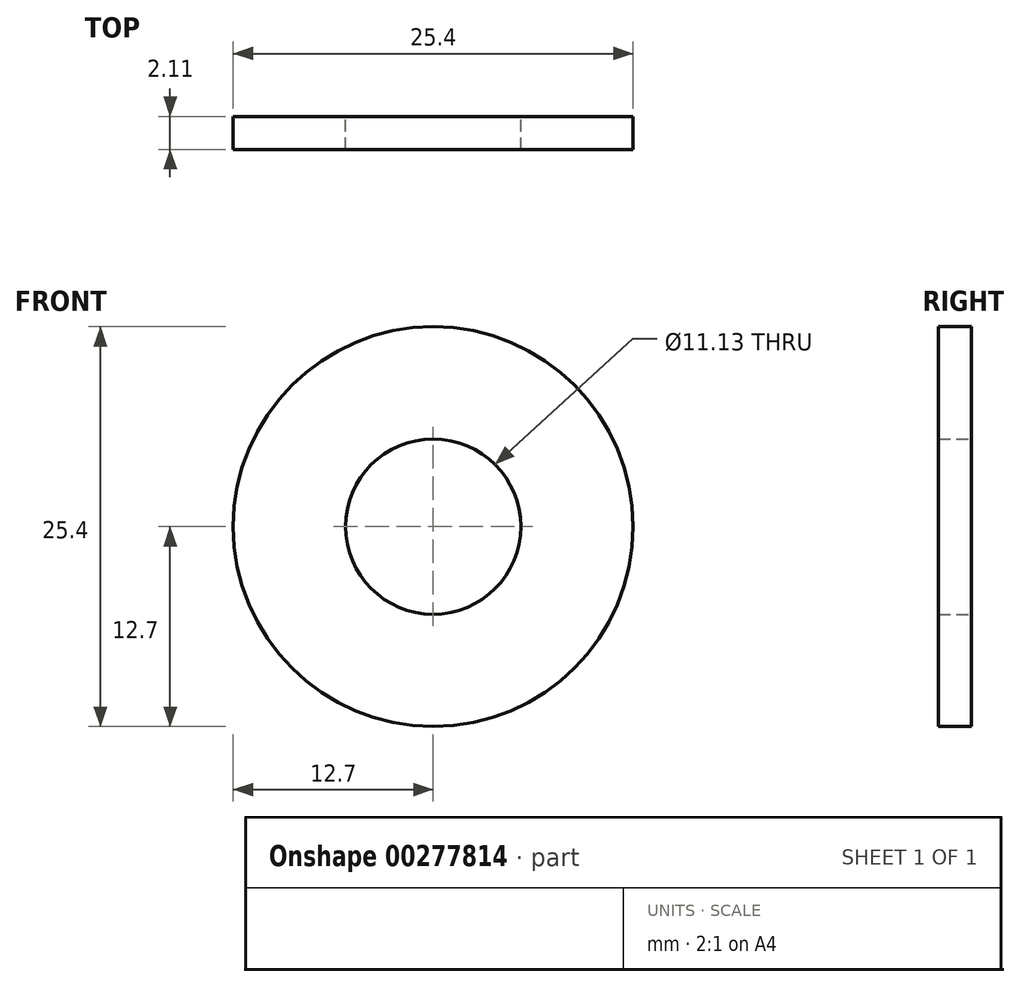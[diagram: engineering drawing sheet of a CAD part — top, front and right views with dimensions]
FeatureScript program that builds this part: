
annotation { "Feature Type Name" : "Feature", "Feature Type Description" : "" }
export const myFeature = defineFeature(function(context is Context, id is Id, definition is map)
    precondition{}
    {
        {
            var Q0;
            Q0=qCreatedBy(makeId("Front.planeOp"),FACE);
            var sketch = newSketch(context, id + "F0", { "sketchPlane" : qUnion([Q0])});
            skCircle(sketch, "E0", {"center": v(0, 0) * mm, "radius": 5.56 * mm});
            skCircle(sketch, "E1", {"center": v(0, 0) * mm, "radius": 12.7 * mm});
            skSolve(sketch);
        }
        {
            var Q0;
            Q0=makeQuery(id+"F0.imprint","IMPRINT",FACE,{"disambiguationData":[TD([[makeQuery(id+"F0.imprint","IMPRINT",EDGE,{"derivedFrom":sQuery(id+"F0.wireOp",EDGE,"E0")}),-1.0]])]});
            extrude(context, id + "F1", {"entities" : qUnion([Q0]), "depth" : 2.1 * mm});
        }
    });
